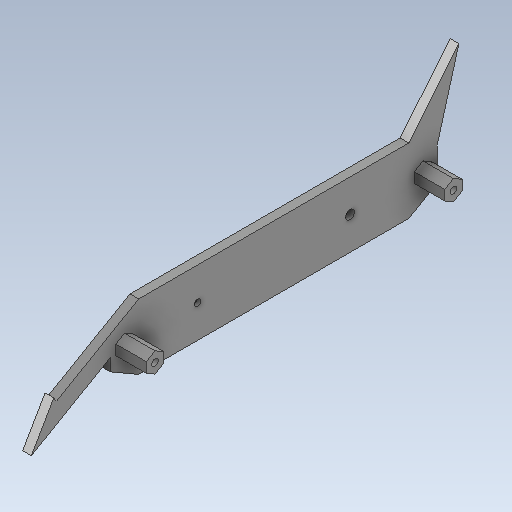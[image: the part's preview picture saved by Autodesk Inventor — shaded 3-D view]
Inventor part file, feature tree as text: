
AUTODESK INVENTOR PART (.ipt)
format: ipt  version: 2020 (Build 240168000, 168)  size: 182,784 bytes
history: native  units: in
note: dims shown in document units (in); Inventor stores cm internally (conversion verified against a paired STEP export)
features: other x3, extrude x2, sketch x2
ambient origin geometry x8: Origin, YZ Plane, XZ Plane, XY Plane, X Axis, Y Axis, Z Axis, Center Point
bodies: Solid1 (feature_tree)
feature tree (7):
  other  "HexWheelGuard.ipt"
  extrude  "Extrusion1"  TaperAngle=0.0deg  [1 undecoded]
  extrude  "Extrusion2"  Depth=0.3937in
  other  "Solid1::HexWheelGuard.ipt"
  other  "TaggingFeature1"
  sketch  "Sketch1"  dims[d0=0.3937in d6=0.0in d7=0.0in]
  sketch  "Sketch2"  dims[d9=0.315in d10=1.4843in d11=60.0deg d12=0.0787in d13=0.3937in d14=0.0in d20=0.3937in d21=0.3937in d22=1.1024in]
note: 1 required parameter value undecoded (feature->parameter linkage not recoverable at this tier; creation-order binding heuristic only, values carry confidence <= 0.55)
